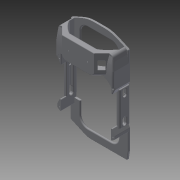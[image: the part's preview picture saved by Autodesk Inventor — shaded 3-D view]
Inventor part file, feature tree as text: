
AUTODESK INVENTOR PART (.ipt)
format: ipt  version: 2015 (Build 190159000, 159)  size: 1,506,304 bytes
history: native  units: mm
features: fillet x47, extrude x34, sketch x26, chamfer x7
ambient origin geometry x8: Origin, YZ Plane, XZ Plane, XY Plane, X Axis, Y Axis, Z Axis, Center Point
bodies: Body1 (feature_tree)
feature tree (114):
  sketch  "Sketch1"  dims[d35=5.0mm d36=0.0mm d40=5.0mm d41=0.0mm]
  extrude  "Extrusion3"  Depth=5.0mm TaperAngle=0.0deg
  extrude  "Extrusion4"  Depth=5.0mm TaperAngle=0.0deg
  fillet  "Fillet1"  Radius=56.0mm
  extrude  "Extrusion5"  Depth=5.0mm
  extrude  "Extrusion6"  Depth=5.0mm TaperAngle=0.0deg
  extrude  "Extrusion7"  Depth=5.0mm
  sketch  "Sketch3"  dims[d46=5.0mm d47=5.0mm]
  extrude  "Extrusion8"  Depth=151.0mm
  extrude  "Extrusion17"  Depth=5.0mm TaperAngle=0.0deg
  extrude  "Extrusion18"  Depth=5.0mm
  extrude  "Extrusion19"  Depth=100.0mm
  sketch  "Sketch17"  dims[d85=5.0mm d86=48.5mm d87=0.0mm]
  extrude  "Extrusion20"  Depth=10.0mm
  extrude  "Extrusion21"  Depth=10.0mm
  sketch  "Sketch18"  dims[d88=5.0mm d89=0.0mm d90=3.0mm]
  extrude  "Extrusion22"  Depth=10.0mm
  extrude  "Extrusion23"  Depth=5.0mm TaperAngle=0.0deg
  extrude  "Extrusion24"  Depth=10.0mm
  extrude  "Extrusion25"  Depth=10.0mm
  fillet  "Fillet3"  Radius=10.0mm
  extrude  "Extrusion26"  Depth=5.0mm TaperAngle=0.0deg
  sketch  "Sketch23"  dims[d97=10.0mm d99=10.0mm]
  extrude  "Extrusion27"  Depth=10.0mm
  extrude  "Extrusion28"  Depth=10.0mm
  sketch  "Sketch24"  dims[d100=10.0mm d102=10.0mm]
  sketch  "Sketch25"  dims[d104=10.0mm d105=5.0mm d106=0.0mm]
  extrude  "Extrusion33"  Depth=40.0mm TaperAngle=0.0deg
  chamfer  "Chamfer1"  Distance=45.0mm
  fillet  "Fillet4"  Radius=9.0mm
  chamfer  "Chamfer2"  Distance=4.0mm
  chamfer  "Chamfer3"  Distance=5.0mm
  chamfer  "Chamfer4"  Distance=16.0mm Angle=45.0deg
  chamfer  "Chamfer5"  Distance=10.0mm
  chamfer  "Chamfer6"  Distance=4.0mm Angle=45.0deg
  chamfer  "Chamfer7"  Distance=5.65mm Angle=45.0deg
  extrude  "Extrusion35"  Depth=1.0mm TaperAngle=45.0deg
  extrude  "Extrusion36"  Depth=1.0mm TaperAngle=45.0deg
  fillet  "Fillet5"  Radius=2.724mm
  fillet  "Fillet6"  Radius=2.663mm
  fillet  "Fillet7"  Radius=5.0mm
  fillet  "Fillet8"  Radius=37.0mm
  fillet  "Fillet9"  Radius=20.0mm
  fillet  "Fillet10"  Radius=2.0mm
  fillet  "Fillet11"  Radius=5.0mm
  fillet  "Fillet12"  Radius=2.0mm
  fillet  "Fillet14"  Radius=2.0mm
  fillet  "Fillet15"  Radius=10.0mm
  fillet  "Fillet16"  Radius=2.0mm
  fillet  "Fillet17"  Radius=2.0mm
  fillet  "Fillet18"  Radius=8.0mm
  fillet  "Fillet19"  Radius=300.0mm
  fillet  "Fillet20"  Radius=1.0mm
  fillet  "Fillet21"  Radius=4.0mm
  fillet  "Fillet22"  Radius=4.0mm
  fillet  "Fillet23"  Radius=4.0mm
  fillet  "Fillet24"  Radius=3.5mm
  fillet  "Fillet25"  Radius=1.0mm
  fillet  "Fillet26"  Radius=4.0mm
  fillet  "Fillet27"  Radius=10.0mm
  fillet  "Fillet28"  Radius=2.0mm
  extrude  "Extrusion37"  Depth=1.0mm
  fillet  "Fillet29"  Radius=2.0mm
  fillet  "Fillet30"  Radius=2.0mm
  fillet  "Fillet31"  Radius=3.0mm
  fillet  "Fillet32"  Radius=4.0mm
  fillet  "Fillet33"  Radius=2.0mm
  fillet  "Fillet34"  Radius=3.0mm
  fillet  "Fillet35"  Radius=3.0mm
  extrude  "Extrusion38"  Depth=1.0mm
  fillet  "Fillet36"  Radius=2.0mm
  extrude  "Extrusion40"  Depth=1.0mm
  fillet  "Fillet37"  Radius=2.0mm
  extrude  "Extrusion41"  Depth=1.0mm
  fillet  "Fillet38"  Radius=21.0mm
  fillet  "Fillet39"  Radius=20.75mm
  extrude  "Extrusion42"  Depth=1.0mm
  sketch  "Sketch32"  dims[d124=40.0mm d125=0.0mm d126=45.0mm d127=0.0mm]
  sketch  "Sketch33"  dims[d129=80.0mm]
  sketch  "Sketch34"  dims[d132=116.0mm]
  sketch  "Sketch35"  dims[d133=32.0mm d134=45.0mm d135=0.0mm d142=9.0mm]
  extrude  "Extrusion43"  Depth=1.0mm
  extrude  "Extrusion44"  Depth=1.0mm
  extrude  "Extrusion45"  Depth=1.0mm TaperAngle=0.0deg
  extrude  "Extrusion46"  Depth=1.0mm
  extrude  "Extrusion47"  Depth=1.0mm TaperAngle=0.0deg
  fillet  "Fillet41"  Radius=1.3mm
  extrude  "Extrusion48"  Depth=1.0mm
  fillet  "Fillet42"  Radius=3.0mm
  fillet  "Fillet43"  Radius=3.0mm
  fillet  "Fillet44"  Radius=3.0mm
  fillet  "Fillet45"  Radius=3.0mm
  fillet  "Fillet46"  Radius=40.0mm
  extrude  "Extrusion49"  Depth=1.0mm TaperAngle=0.0deg
  extrude  "Extrusion50"  Depth=1.0mm TaperAngle=0.0deg
  fillet  "Fillet47"  Radius=20.0mm
  fillet  "Fillet48"  Radius=20.0mm
  fillet  "Fillet49"  Radius=8.0mm
  fillet  "Fillet50"  Radius=100.0mm
  sketch  "Sketch2"  dims[d42=20.0mm d43=5.0mm d44=0.0mm d45=56.0mm]
  sketch  "Sketch14"  dims[d48=5.0mm d49=45.0mm d50=0.0mm]
  sketch  "Sketch15"  dims[d51=5.0mm d52=0.0mm d54=35.0mm]
  sketch  "Sketch16"  dims[d55=35.0mm d56=0.0mm d84=151.0mm]
  sketch  "Sketch20"  dims[d91=3.0mm d92=100.0mm]
  sketch  "Sketch22"  dims[d93=5.0mm d94=0.0mm d95=10.0mm]
  sketch  "Sketch26"  dims[d107=5.0mm d108=0.0mm d109=10.0mm]
  sketch  "Sketch28"  dims[d111=10.0mm d113=10.0mm d114=10.0mm]
  sketch  "Sketch29"  dims[d116=10.0mm d117=5.0mm d118=0.0mm]
  sketch  "Sketch30"  dims[d119=5.0mm d120=0.0mm d121=10.0mm]
  sketch  "Sketch31"  dims[d122=10.0mm d123=10.0mm]
  sketch  "Sketch36"  dims[d143=45.0mm]
  sketch  "Sketch37"  dims[d144=45.0mm d145=4.0mm d146=0.0mm]
  sketch  "Sketch38"  dims[d147=4.0mm d148=5.0mm d149=0.0mm d150=0.0mm]
  sketch  "Sketch39"  dims[d163=90.0mm d174=5.0mm d175=0.0mm d178=16.0mm d179=2.0mm d180=45.0deg d181=10.0mm d182=4.0mm d183=2.0mm d184=45.0deg d185=5.65mm d186=2.0mm d187=45.0deg d188=10.43mm d189=2.0mm d190=45.0deg d191=10.43mm d192=2.0mm d193=45.0deg d194=2.724mm d195=2.0mm d196=45.0deg d197=2.663mm d198=2.0mm d199=45.0deg d200=5.0mm d201=0.0mm d202=37.0mm d203=0.0mm d204=20.0mm d205=2.0mm d206=5.0mm d207=2.0mm d208=2.0mm d209=10.0mm d210=2.0mm d211=2.0mm d213=8.0mm d214=300.0mm d215=1.0mm d216=4.0mm d217=4.0mm d218=4.0mm d219=3.5mm d220=1.0mm d221=4.0mm d222=10.0mm d223=2.0mm d224=2.0mm d225=2.0mm d226=2.0mm d227=3.0mm d228=4.0mm d229=0.0mm d230=2.0mm d231=3.0mm d232=3.0mm d233=4.0mm d234=2.0mm d235=3.0mm d236=2.0mm d237=15.0mm d238=21.0mm d239=20.75mm d240=0.0mm d241=1.0mm d242=122.0mm d245=135.3mm d246=20.75mm d247=0.0mm d248=1.0mm d249=20.0mm d250=0.0mm d251=1.3mm d252=0.2mm d257=3.0mm d258=3.0mm d262=3.0mm d263=3.0mm d264=40.0mm d265=0.0mm d266=20.0mm d267=0.0mm d268=20.0mm d269=0.0mm d270=20.0mm d271=0.0mm d272=20.0mm d273=0.0mm d274=8.0mm d275=100.0mm d276=35.0mm d277=0.0mm d279=2.0mm d280=8.0mm d281=100.0mm d282=35.0mm d283=0.0mm d284=2.0mm d285=2.0mm d286=2.0mm d287=2.0mm d288=2.0mm d290=16.0mm d291=16.0mm d292=3.0mm d293=3.0mm d294=15.0mm d295=0.0mm d297=5.0mm d298=0.0mm d299=2.0mm d300=40.0mm d301=1.0mm d302=1.0mm]
